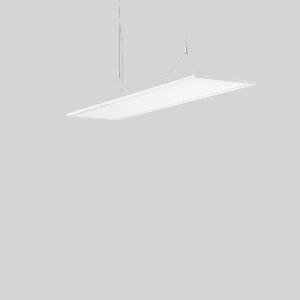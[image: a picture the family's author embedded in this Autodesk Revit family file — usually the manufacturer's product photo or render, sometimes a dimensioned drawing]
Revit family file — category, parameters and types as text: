
# Revit family: sidelite_eco_312371_002_76_1251
name_source: partatom
category: Lighting Fixtures
units: mm (PartAtom-declared; Revit-internal decimal feet)

## family parameters
Cut with Voids When Loaded = No
Host = Face
Light Source = No
Part Type = Normal
Room Calculation Point = No
Round Connector Dimension = Use Diameter
Shared = No

## types (1)
- SIDELITE ECO (1 x LED Modul 830, 3300 lm, 3000)
    Apparent Load = 29 VA
    Approval mark = CE
    CIE Flux Codes = 46 79 96 100 100
    Color Rendering = 80
    Color Temperature = 3000
    Default Elevation = 1800 mm
    Description = Series: SIDELITE ECO
Aesthetically pleasing pendant-mounted surface luminaire with extremely flat profile and progressive LED technology. Frame made of aluminium, powder-coated. Diffuser: plastic, opal. Lightguide and diffuser made of non-yellowing plastic (PMMA). Lateral light emission (RZB SIDELITE technology) for homogeneous light distribution. 2-point steel cable suspension, steplessly adjustable. Converter in the canopy. 
Colour: white
Length: 1195 mm
Width: 295 mm
Height: 12 mm
Suspension length: 300-1500 mm
Lamp: LED
Socket: without socket
Colour temperature: 3000K
Colour rendering index (CRI): 80
System power: 29 W
Rated luminous flux: 3300 lm
Beam angle Down: 122° / 112°
Luminous efficiency: 114 lm/W
Control gear: Converter, dimmable, DALI
Protection class: II
Type of protection: IP 20
    Height = 12 mm  [stored 0.0393701 ft]
    Lamp = 1 x LED Modul 830
    Lamp Light Flux = 3300 lm
    Lamp count = 1
    Length = 1195 mm
    Lifetime = 50000 h
    Luminous efficacy = 114 lm/W
    Manufacturer = RZB
    ModVariant = No
    Model = 312371.002.76
    Mounting Place = Ceiling
    Mounting Type = Pendant
    Number of Poles = 1
    OnlyDefault = Yes
    Power Factor = 1
    Product Name = SIDELITE ECO
    Product group = Pendant modular luminaires
    ProductGroupID = 906
    Protection Class = Protection class II
    Protection Degree = IP 20
    RLX_Detail_Level = 1
    RLX_Emergency_Light_Flux = 0 lm
    RLX_Emergency_Type = 0
    RLX_Emergency_Type_DB = No
    RlxData = <blob elided: 19253 chars, md5=10422b20>
    Socket = socket
    Standby Power = 0 W
    System Light Flux = 3300 lm
    System Power = 29 W
    Type Comments = ALEA SPOT
    Type Image = 312371.002.jpg
    URL = http://relux.com
    VarID = ---
    Voltage = 230 V
    Voltage Range = 220-240 V
    Weight = 0.00 kg
    Width = 295 mm

note: [stored X ft] marks values corroborated as IEEE doubles in the binary element streams (Revit-internal decimal feet)

## geometry (parser evidence)
native form markers: Blend x4, Sweep x10
no freeform markers — native parametric forms only
